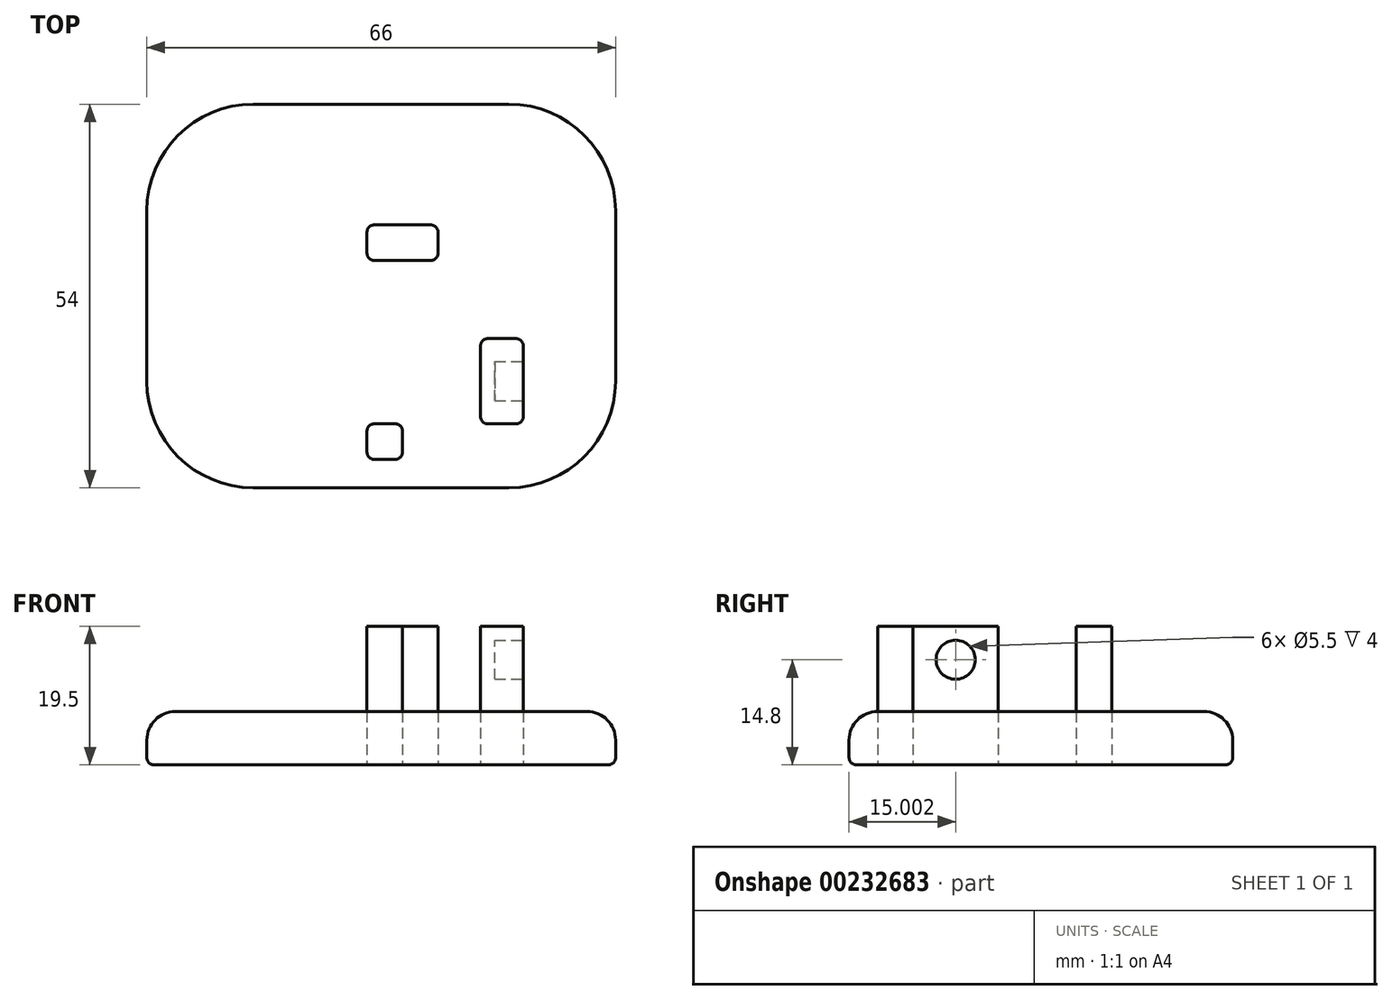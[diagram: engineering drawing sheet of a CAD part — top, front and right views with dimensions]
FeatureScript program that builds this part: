
annotation { "Feature Type Name" : "Feature", "Feature Type Description" : "" }
export const myFeature = defineFeature(function(context is Context, id is Id, definition is map)
    precondition{}
    {
        {
            var Q0;
            Q0=qCreatedBy(makeId("Top.planeOp"),FACE);
            var sketch = newSketch(context, id + "F0", { "sketchPlane" : qUnion([Q0])});
            skLineSegment(sketch, "E0.bottom", {"start": v(-30.44, 33.23) * mm, "end": v(35.56, 33.23) * mm});
            skLineSegment(sketch, "E0.top", {"start": v(-30.44, -20.77) * mm, "end": v(35.56, -20.77) * mm});
            skLineSegment(sketch, "E0.left", {"start": v(-30.44, 33.23) * mm, "end": v(-30.44, -20.77) * mm});
            skLineSegment(sketch, "E0.right", {"start": v(35.56, 33.23) * mm, "end": v(35.56, -20.77) * mm});
            skSolve(sketch);
        }
        {
            var Q0;
            Q0=makeQuery(id+"F0.imprint","IMPRINT",FACE,{"disambiguationData":[TD([[makeQuery(id+"F0.imprint","IMPRINT",EDGE,{"derivedFrom":sQuery(id+"F0.wireOp",EDGE,"E0.bottom")}),-1.0]])]});
            extrude(context, id + "F1", {"entities" : qUnion([Q0]), "depth" : 7.5 * mm});
        }
        {
            var Q0;
            Q0=makeQuery(id+"F1.opExtrude","CAP_FACE",FACE,{"disambiguationData":[OSD([sQuery(id+"F0.wireOp",EDGE,"E0.bottom"),sQuery(id+"F0.wireOp",EDGE,"E0.top"),sQuery(id+"F0.wireOp",EDGE,"E0.left"),sQuery(id+"F0.wireOp",EDGE,"E0.right")])],"isStart":false});
            fillet(context, id + "F2", {"entities" : qUnion([Q0]), "radius" : 4 * mm, "tangentPropagation" : true, "allowEdgeOverflow" : false});
        }
        {
            var Q0;
            Q0=makeQuery(id+"F1.opExtrude","CAP_FACE",FACE,{"disambiguationData":[OSD([sQuery(id+"F0.wireOp",EDGE,"E0.bottom"),sQuery(id+"F0.wireOp",EDGE,"E0.top"),sQuery(id+"F0.wireOp",EDGE,"E0.left"),sQuery(id+"F0.wireOp",EDGE,"E0.right")])],"isStart":true});
            fillet(context, id + "F3", {"entities" : qUnion([Q0]), "radius" : 1 * mm, "tangentPropagation" : true, "allowEdgeOverflow" : false});
        }
        {
            var Q0;
            Q0=qCreatedBy(makeId("Top.planeOp"),FACE);
            var sketch = newSketch(context, id + "F4", { "sketchPlane" : qUnion([Q0])});
            skLineSegment(sketch, "E1.bottom", {"start": v(16.56, 0.23) * mm, "end": v(22.56, 0.23) * mm});
            skLineSegment(sketch, "E1.top", {"start": v(16.56, -11.77) * mm, "end": v(22.56, -11.77) * mm});
            skLineSegment(sketch, "E1.left", {"start": v(16.56, 0.23) * mm, "end": v(16.56, -11.77) * mm});
            skLineSegment(sketch, "E1.right", {"start": v(22.56, 0.23) * mm, "end": v(22.56, -11.77) * mm});
            skLineSegment(sketch, "E2.bottom", {"start": v(0.56, 16.23) * mm, "end": v(10.56, 16.23) * mm});
            skLineSegment(sketch, "E2.top", {"start": v(0.56, 11.23) * mm, "end": v(10.56, 11.23) * mm});
            skLineSegment(sketch, "E2.left", {"start": v(0.56, 16.23) * mm, "end": v(0.56, 11.23) * mm});
            skLineSegment(sketch, "E2.right", {"start": v(10.56, 16.23) * mm, "end": v(10.56, 11.23) * mm});
            skLineSegment(sketch, "E3.bottom", {"start": v(0.56, -11.77) * mm, "end": v(5.56, -11.77) * mm});
            skLineSegment(sketch, "E3.top", {"start": v(0.56, -16.77) * mm, "end": v(5.56, -16.77) * mm});
            skLineSegment(sketch, "E3.left", {"start": v(0.56, -11.77) * mm, "end": v(0.56, -16.77) * mm});
            skLineSegment(sketch, "E3.right", {"start": v(5.56, -11.77) * mm, "end": v(5.56, -16.77) * mm});
            skLineSegment(sketch, "E4", {"start": v(-0.15, -11.77) * mm, "end": v(16.56, -11.77) * mm, "construction": true});
            skLineSegment(sketch, "E5", {"start": v(0.56, 31.2) * mm, "end": v(0.56, -45.77) * mm, "construction": true});
            skSolve(sketch);
        }
        {
            var Q0;
            Q0=qSketchRegion(id+"F4",true);
            extrude(context, id + "F5", {"entities" : qUnion([Q0]), "depth" : 19.5 * mm});
        }
        {
            var Q0;
            Q0=makeQuery(id+"F5.opExtrude","SWEPT_EDGE",EDGE,{"disambiguationData":[OSD([sQuery(id+"F4.wireOp",EDGE,"E1.top"),sQuery(id+"F4.wireOp",EDGE,"E1.left")])]});
            var Q1;
            Q1=makeQuery(id+"F5.opExtrude","SWEPT_EDGE",EDGE,{"disambiguationData":[OSD([sQuery(id+"F4.wireOp",EDGE,"E1.top"),sQuery(id+"F4.wireOp",EDGE,"E1.right")])]});
            var Q2;
            Q2=makeQuery(id+"F5.opExtrude","SWEPT_EDGE",EDGE,{"disambiguationData":[OSD([sQuery(id+"F4.wireOp",EDGE,"E3.top"),sQuery(id+"F4.wireOp",EDGE,"E3.left")])]});
            var Q3;
            Q3=makeQuery(id+"F5.opExtrude","SWEPT_EDGE",EDGE,{"disambiguationData":[OSD([sQuery(id+"F4.wireOp",EDGE,"E3.top"),sQuery(id+"F4.wireOp",EDGE,"E3.right")])]});
            var Q4;
            Q4=makeQuery(id+"F5.opExtrude","SWEPT_EDGE",EDGE,{"disambiguationData":[OSD([sQuery(id+"F4.wireOp",EDGE,"E2.top"),sQuery(id+"F4.wireOp",EDGE,"E2.right")])]});
            var Q5;
            Q5=makeQuery(id+"F5.opExtrude","SWEPT_EDGE",EDGE,{"disambiguationData":[OSD([sQuery(id+"F4.wireOp",EDGE,"E2.top"),sQuery(id+"F4.wireOp",EDGE,"E2.left")])]});
            var Q6;
            Q6=makeQuery(id+"F5.opExtrude","SWEPT_EDGE",EDGE,{"disambiguationData":[OSD([sQuery(id+"F4.wireOp",EDGE,"E3.bottom"),sQuery(id+"F4.wireOp",EDGE,"E3.right")])]});
            var Q7;
            Q7=makeQuery(id+"F5.opExtrude","SWEPT_EDGE",EDGE,{"disambiguationData":[OSD([sQuery(id+"F4.wireOp",EDGE,"E1.bottom"),sQuery(id+"F4.wireOp",EDGE,"E1.right")])]});
            var Q8;
            Q8=makeQuery(id+"F5.opExtrude","SWEPT_EDGE",EDGE,{"disambiguationData":[OSD([sQuery(id+"F4.wireOp",EDGE,"E2.bottom"),sQuery(id+"F4.wireOp",EDGE,"E2.right")])]});
            var Q9;
            Q9=makeQuery(id+"F5.opExtrude","SWEPT_EDGE",EDGE,{"disambiguationData":[OSD([sQuery(id+"F4.wireOp",EDGE,"E2.bottom"),sQuery(id+"F4.wireOp",EDGE,"E2.left")])]});
            var Q10;
            Q10=makeQuery(id+"F5.opExtrude","SWEPT_EDGE",EDGE,{"disambiguationData":[OSD([sQuery(id+"F4.wireOp",EDGE,"E1.bottom"),sQuery(id+"F4.wireOp",EDGE,"E1.left")])]});
            var Q11;
            Q11=makeQuery(id+"F5.opExtrude","SWEPT_EDGE",EDGE,{"disambiguationData":[OSD([sQuery(id+"F4.wireOp",EDGE,"E3.bottom"),sQuery(id+"F4.wireOp",EDGE,"E3.left")])]});
            fillet(context, id + "F6", {"entities" : qUnion([Q0, Q1, Q2, Q3, Q4, Q5, Q6, Q7, Q8, Q9, Q10, Q11]), "radius" : 1 * mm, "tangentPropagation" : true, "allowEdgeOverflow" : false});
        }
        {
            var Q0;
            Q0=makeQuery(id+"F5.opExtrude","SWEPT_FACE",FACE,{"disambiguationData":[OSD([sQuery(id+"F4.wireOp",EDGE,"E1.right")])]});
            var sketch = newSketch(context, id + "F7", { "sketchPlane" : qUnion([Q0])});
            skCircle(sketch, "E6", {"center": v(-5.77, 14.8) * mm, "radius": 2.75 * mm});
            skLineSegment(sketch, "E7", {"start": v(-5.77, 19.5) * mm, "end": v(-5.77, -11.56) * mm, "construction": true});
            skPoint(sketch, "E7.endSnap0", {"position": v(-5.77, 0) * mm});
            skSolve(sketch);
        }
        {
            var Q0;
            Q0=makeQuery(id+"F7.imprint","IMPRINT",FACE,{"disambiguationData":[TD([[makeQuery(id+"F7.imprint","IMPRINT",EDGE,{"derivedFrom":sQuery(id+"F7.wireOp",EDGE,"E6")}),1.0]])]});
            extrude(context, id + "F8", {"entities" : qUnion([Q0]), "operationType" : NewBodyOperationType.REMOVE, "oppositeDirection" : true, "depth" : 4 * mm});
        }
        {
            var Q0;
            Q0=makeQuery(id+"F1.opExtrude","SWEPT_EDGE",EDGE,{"disambiguationData":[OSD([sQuery(id+"F0.wireOp",EDGE,"E0.top"),sQuery(id+"F0.wireOp",EDGE,"E0.right")])]});
            var Q1;
            Q1=makeQuery(id+"F1.opExtrude","SWEPT_EDGE",EDGE,{"disambiguationData":[OSD([sQuery(id+"F0.wireOp",EDGE,"E0.bottom"),sQuery(id+"F0.wireOp",EDGE,"E0.right")])]});
            var Q2;
            Q2=makeQuery(id+"F1.opExtrude","SWEPT_EDGE",EDGE,{"disambiguationData":[OSD([sQuery(id+"F0.wireOp",EDGE,"E0.bottom"),sQuery(id+"F0.wireOp",EDGE,"E0.left")])]});
            var Q3;
            Q3=makeQuery(id+"F1.opExtrude","SWEPT_EDGE",EDGE,{"disambiguationData":[OSD([sQuery(id+"F0.wireOp",EDGE,"E0.top"),sQuery(id+"F0.wireOp",EDGE,"E0.left")])]});
            fillet(context, id + "F9", {"entities" : qUnion([Q0, Q1, Q2, Q3]), "radius" : 15 * mm, "tangentPropagation" : true, "allowEdgeOverflow" : false});
        }
    });
